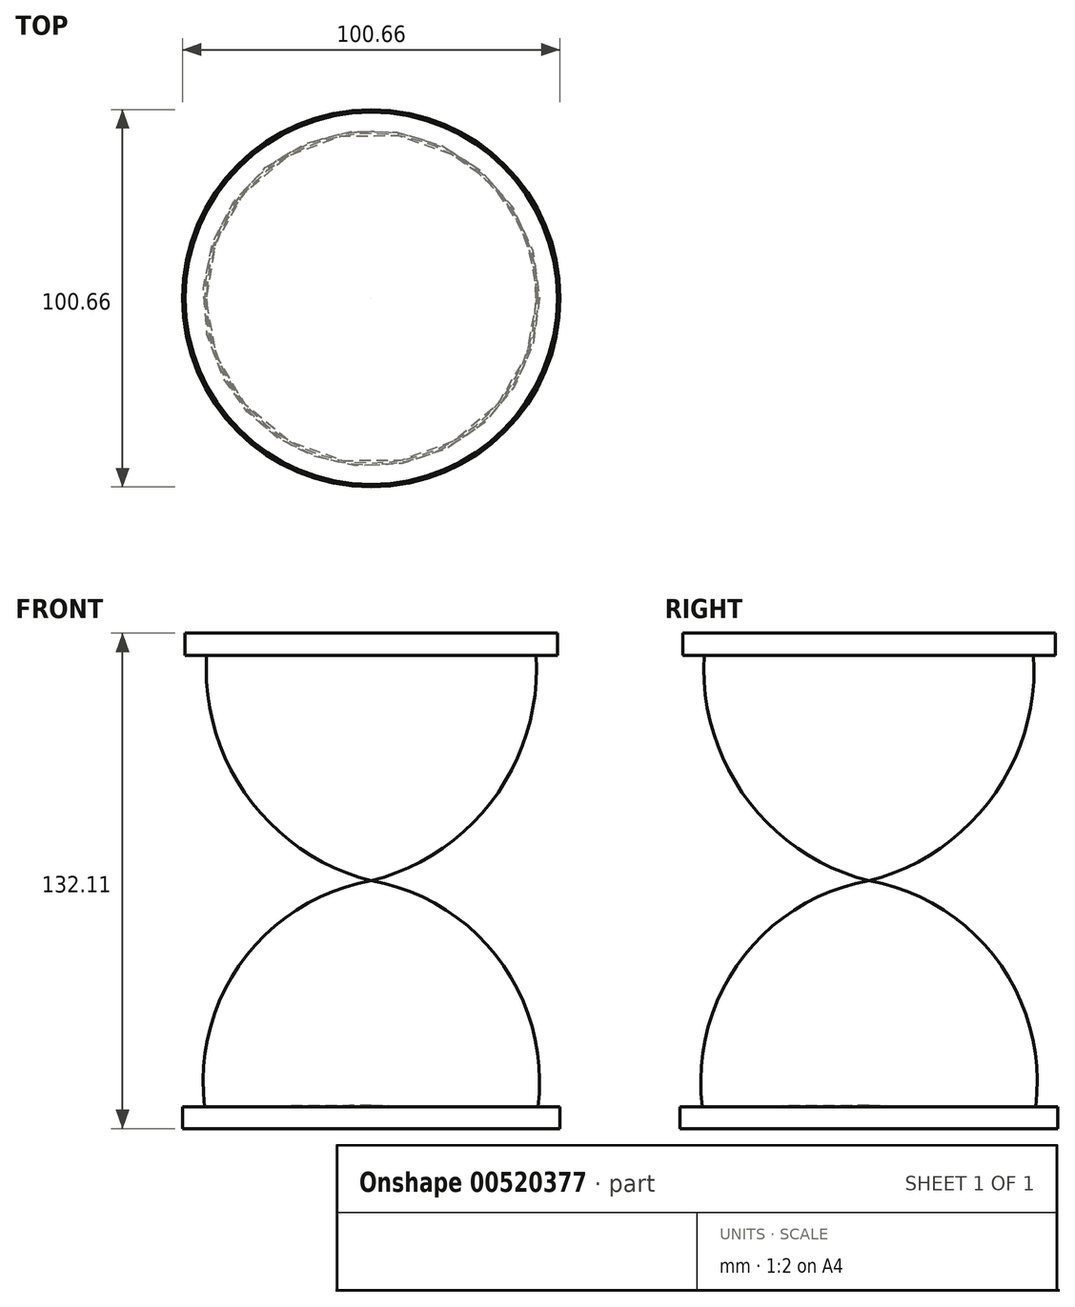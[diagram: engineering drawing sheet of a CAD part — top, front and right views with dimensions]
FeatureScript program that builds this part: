
annotation { "Feature Type Name" : "Feature", "Feature Type Description" : "" }
export const myFeature = defineFeature(function(context is Context, id is Id, definition is map)
    precondition{}
    {
        {
            var Q0;
            Q0=qCreatedBy(makeId("Front.planeOp"),FACE);
            var sketch = newSketch(context, id + "F0", { "sketchPlane" : qUnion([Q0])});
            skLineSegment(sketch, "E0", {"start": v(0, 87.91) * mm, "end": v(0, -90.06) * mm, "construction": true});
            skLineSegment(sketch, "E1", {"start": v(0, 66) * mm, "end": v(49.64, 66) * mm});
            skLineSegment(sketch, "E2", {"start": v(49.64, 66) * mm, "end": v(49.64, 60.1) * mm});
            skLineSegment(sketch, "E3", {"start": v(49.64, 60.1) * mm, "end": v(0, 60.1) * mm});
            skLineSegment(sketch, "E4", {"start": v(0, 66) * mm, "end": v(0, 60.1) * mm});
            skArc(sketch, "E5", {"start": v(0.01, 0) * mm, "mid": v(32.8, 22.13) * mm, "end": v(43.9, 60.1) * mm});
            skLineSegment(sketch, "E6", {"start": v(50.33, -66.1) * mm, "end": v(0, -66.1) * mm});
            skLineSegment(sketch, "E7", {"start": v(50.33, -66.1) * mm, "end": v(50.33, -60.29) * mm});
            skLineSegment(sketch, "E8", {"start": v(50.33, -60.29) * mm, "end": v(0, -60.29) * mm});
            skArc(sketch, "E9", {"start": v(44.43, -60.29) * mm, "mid": v(34.25, -21.28) * mm, "end": v(0.01, 0) * mm});
            skLineSegment(sketch, "E10", {"start": v(0, -60.29) * mm, "end": v(0, -66.1) * mm});
            skLineSegment(sketch, "E11", {"start": v(44.43, -60.29) * mm, "end": v(0, -60.29) * mm});
            skLineSegment(sketch, "E12", {"start": v(0, -59.94) * mm, "end": v(0, 60.1) * mm});
            skLineSegment(sketch, "E13", {"start": v(0, 60.1) * mm, "end": v(43.9, 60.1) * mm});
            skLineSegment(sketch, "E14", {"start": v(0.01, 0) * mm, "end": v(0, -59.94) * mm});
            skLineSegment(sketch, "E15", {"start": v(0, -59.94) * mm, "end": v(44.43, -60.29) * mm});
            skSolve(sketch);
        }
        {
            var Q0;
            Q0=makeQuery(id+"F0.imprint","IMPRINT",FACE,{"disambiguationData":[TD([[makeQuery(id+"F0.imprint","IMPRINT",EDGE,{"derivedFrom":sQuery(id+"F0.wireOp",EDGE,"E5")}),1.0]])]});
            var Q1;
            Q1=makeQuery(id+"F0.imprint","IMPRINT",FACE,{"disambiguationData":[TD([[makeQuery(id+"F0.imprint","IMPRINT",EDGE,{"derivedFrom":sQuery(id+"F0.wireOp",EDGE,"E1")}),-1.0]])]});
            var Q2;
            Q2=makeQuery(id+"F0.imprint","IMPRINT",FACE,{"disambiguationData":[TD([[makeQuery(id+"F0.imprint","IMPRINT",EDGE,{"derivedFrom":sQuery(id+"F0.wireOp",EDGE,"E9")}),1.0]])]});
            var Q3;
            Q3=makeQuery(id+"F0.imprint","IMPRINT",FACE,{"disambiguationData":[TD([[makeQuery(id+"F0.imprint","IMPRINT",EDGE,{"derivedFrom":sQuery(id+"F0.wireOp",EDGE,"E6")}),-1.0]])]});
            var Q4;
            Q4=sQuery(id+"F0.wireOp",EDGE,"E0");
            revolve(context, id + "F1", {"entities" : qUnion([Q0, Q1, Q2, Q3]), "axis" : qUnion([Q4]), "revolveType" : RevolveType.FULL});
        }
    });
